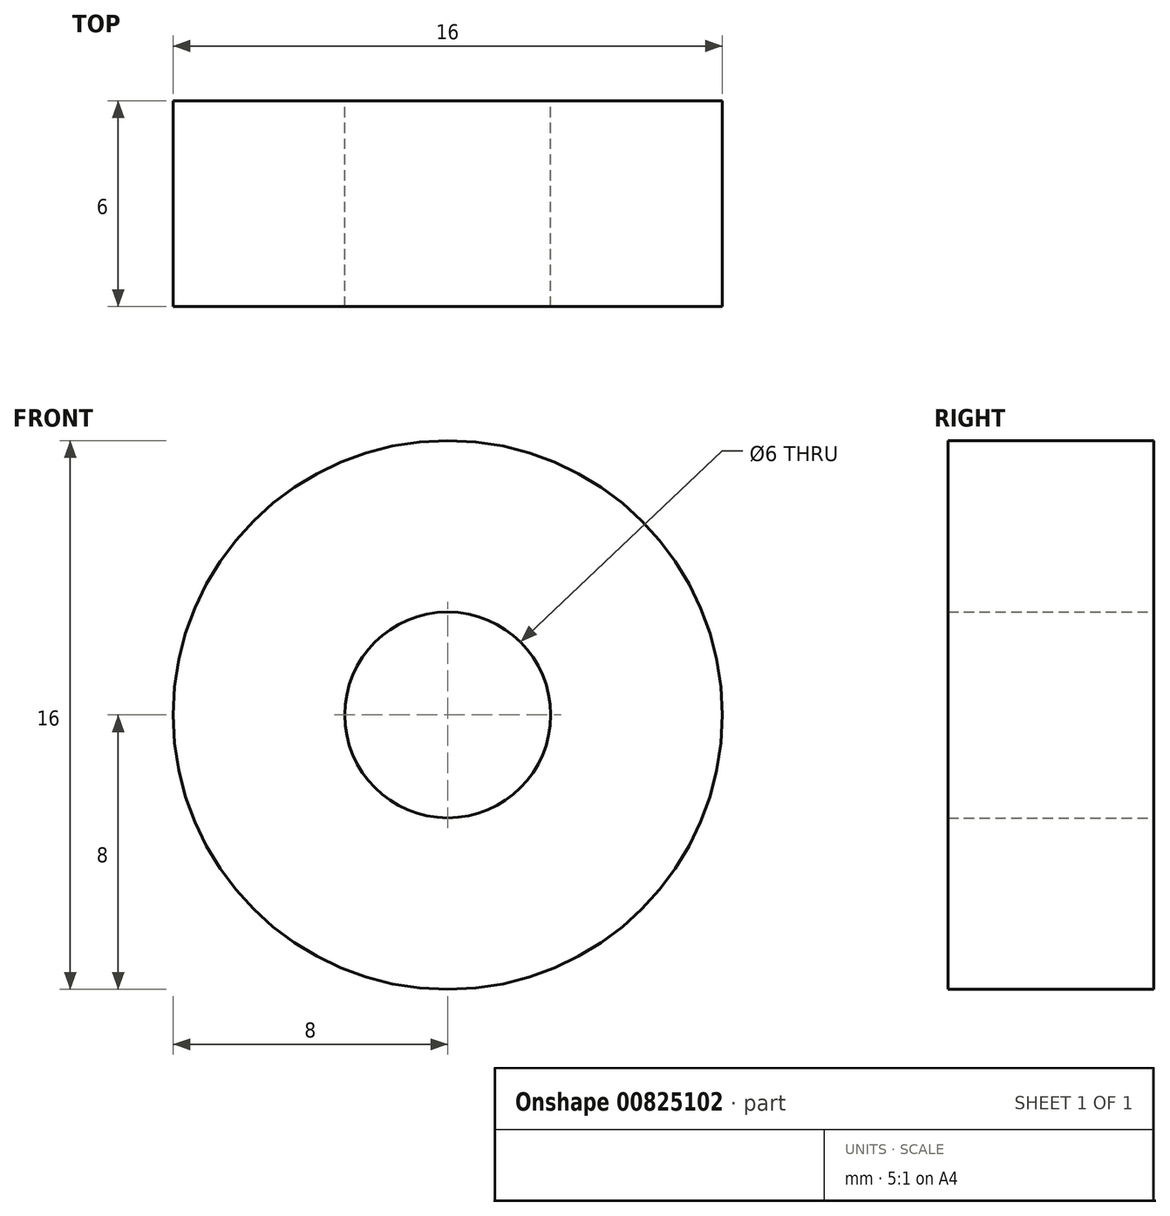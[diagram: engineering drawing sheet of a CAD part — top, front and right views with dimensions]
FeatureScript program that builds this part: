
annotation { "Feature Type Name" : "Feature", "Feature Type Description" : "" }
export const myFeature = defineFeature(function(context is Context, id is Id, definition is map)
    precondition{}
    {
        {
            var Q0;
            Q0=qCreatedBy(makeId("Front.planeOp"),FACE);
            var sketch = newSketch(context, id + "F0", { "sketchPlane" : qUnion([Q0])});
            skCircle(sketch, "E0", {"center": v(0, 0) * mm, "radius": 3 * mm});
            skCircle(sketch, "E1", {"center": v(0, 0) * mm, "radius": 8 * mm});
            skLineSegment(sketch, "E2", {"start": v(0, 0) * mm, "end": v(8, 0) * mm, "construction": true});
            skLineSegment(sketch, "E3", {"start": v(0, 0) * mm, "end": v(0, 8) * mm, "construction": true});
            skLineSegment(sketch, "E4", {"start": v(0, 0) * mm, "end": v(-8, 0) * mm, "construction": true});
            skLineSegment(sketch, "E5", {"start": v(0, 0) * mm, "end": v(0, -8) * mm, "construction": true});
            skSolve(sketch);
        }
        {
            var Q0;
            Q0=makeQuery(id+"F0.imprint","IMPRINT",FACE,{"disambiguationData":[TD([[makeQuery(id+"F0.imprint","IMPRINT",EDGE,{"derivedFrom":sQuery(id+"F0.wireOp",EDGE,"E0")}),-1.0]])]});
            extrude(context, id + "F1", {"entities" : qUnion([Q0]), "depth" : 6 * mm, "offsetDistance" : 25.4 * mm});
        }
    });
